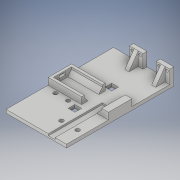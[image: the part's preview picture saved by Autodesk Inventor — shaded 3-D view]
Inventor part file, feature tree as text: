
AUTODESK INVENTOR PART (.ipt)
format: ipt  version: 2018 (Build 220112000, 112)  size: 320,512 bytes
history: native  units: in
note: dims shown in document units (in); Inventor stores cm internally (conversion verified against a paired STEP export)
features: sketch x14, extrude x13, chamfer x3, hole x1
ambient origin geometry x8: Origin, YZ Plane, XZ Plane, XY Plane, X Axis, Y Axis, Z Axis, Center Point
bodies: Solid1 (feature_tree)
feature tree (31):
  extrude  "Extrusion1"  Depth=4.5in
  extrude  "Extrusion2"  Depth=0.5in
  extrude  "Extrusion4"  Depth=0.5in
  extrude  "Extrusion5"  Depth=1.375in
  extrude  "Extrusion6"  Depth=1.75in
  extrude  "Extrusion7"  TaperAngle=0.0deg  [1 undecoded]
  extrude  "Extrusion8"  Depth=1.75in
  extrude  "Extrusion9"  Depth=0.15in
  extrude  "Extrusion10"  Depth=0.5in
  extrude  "Extrusion13"  Depth=0.2in
  extrude  "Extrusion14"  Depth=2.5in TaperAngle=0.0deg
  extrude  "Extrusion15"  Depth=0.3in
  chamfer  "Chamfer1"  Distance=0.3in
  extrude  "Extrusion18"  Depth=0.25in
  chamfer  "Chamfer4"  Distance=0.25in
  chamfer  "Chamfer5"  Distance=0.25in
  hole  "Hole1"  [1 undecoded]
  sketch  "Sketch1"  dims[d0=6.0in d1=4.5in]
  sketch  "Sketch2"  dims[d2=0.5in d3=0.5in]
  sketch  "Sketch4"  dims[d4=0.5in d5=0.5in]
  sketch  "Sketch5"  dims[d6=1.375in d7=1.375in]
  sketch  "Sketch6"  dims[d8=1.75in d9=1.75in]
  sketch  "Sketch7"  dims[d10=0.4in d11=0.0in d12=0.0in]
  sketch  "Sketch8"  dims[d13=0.82in d14=1.75in]
  sketch  "Sketch9"  dims[d15=0.15in d16=0.15in]
  sketch  "Sketch10"  dims[d17=0.5in d18=0.5in]
  sketch  "Sketch13"  dims[d19=0.2in d20=0.2in]
  sketch  "Sketch14"  dims[d21=0.465in d22=2.5in d23=0.0in]
  sketch  "Sketch15"  dims[d24=2.125in d28=0.3in]
  sketch  "Sketch19"  dims[d29=0.3in]
  sketch  "Sketch20"  dims[d30=0.3in d31=0.3in d32=0.25in d33=0.25in d34=0.25in d35=0.25in d36=0.8in d37=1.75in d38=0.8in d39=1.75in d40=0.4in d41=0.0in d42=1.0in d43=0.0in d44=1.0in d45=0.0in d46=0.0in d47=0.0in d48=0.5in d49=0.5in d50=0.0in d51=0.35in d52=0.5in d53=4.0in d54=0.125in d55=0.0in d56=0.15in d57=0.0in d58=2.0in d59=2.0in d60=0.3in d61=0.3in d62=1.0in d63=0.0in d68=0.35in d69=0.35in d70=0.195in d71=0.5in d72=0.0in d73=0.2in d74=0.22in d75=0.175in d76=0.175in d77=0.5in d78=0.0in d79=0.0in d80=0.0in d81=0.392in d82=0.0in d83=0.35in d84=0.125in d85=45.0deg d118=1.0in d119=1.0in d120=1.0in d121=0.3in d122=0.3in d123=0.35in d124=0.3in d125=0.7in d126=0.7in d127=0.3in d128=0.35in d129=1.0in d130=0.0in d131=0.7in d132=1.0in d133=45.0deg d134=0.7in d135=1.0in d136=45.0deg d137=0.2in d138=0.2in d139=0.2in d140=0.2in d141=0.2in d142=0.2in d143=0.2in d144=0.2in d145=0.2in d146=0.75in d147=0.375in d148=0.25in d149=0.5635in d150=1.0in d151=0.8108in]
note: 2 required parameter values undecoded (feature->parameter linkage not recoverable at this tier; creation-order binding heuristic only, values carry confidence <= 0.55)
